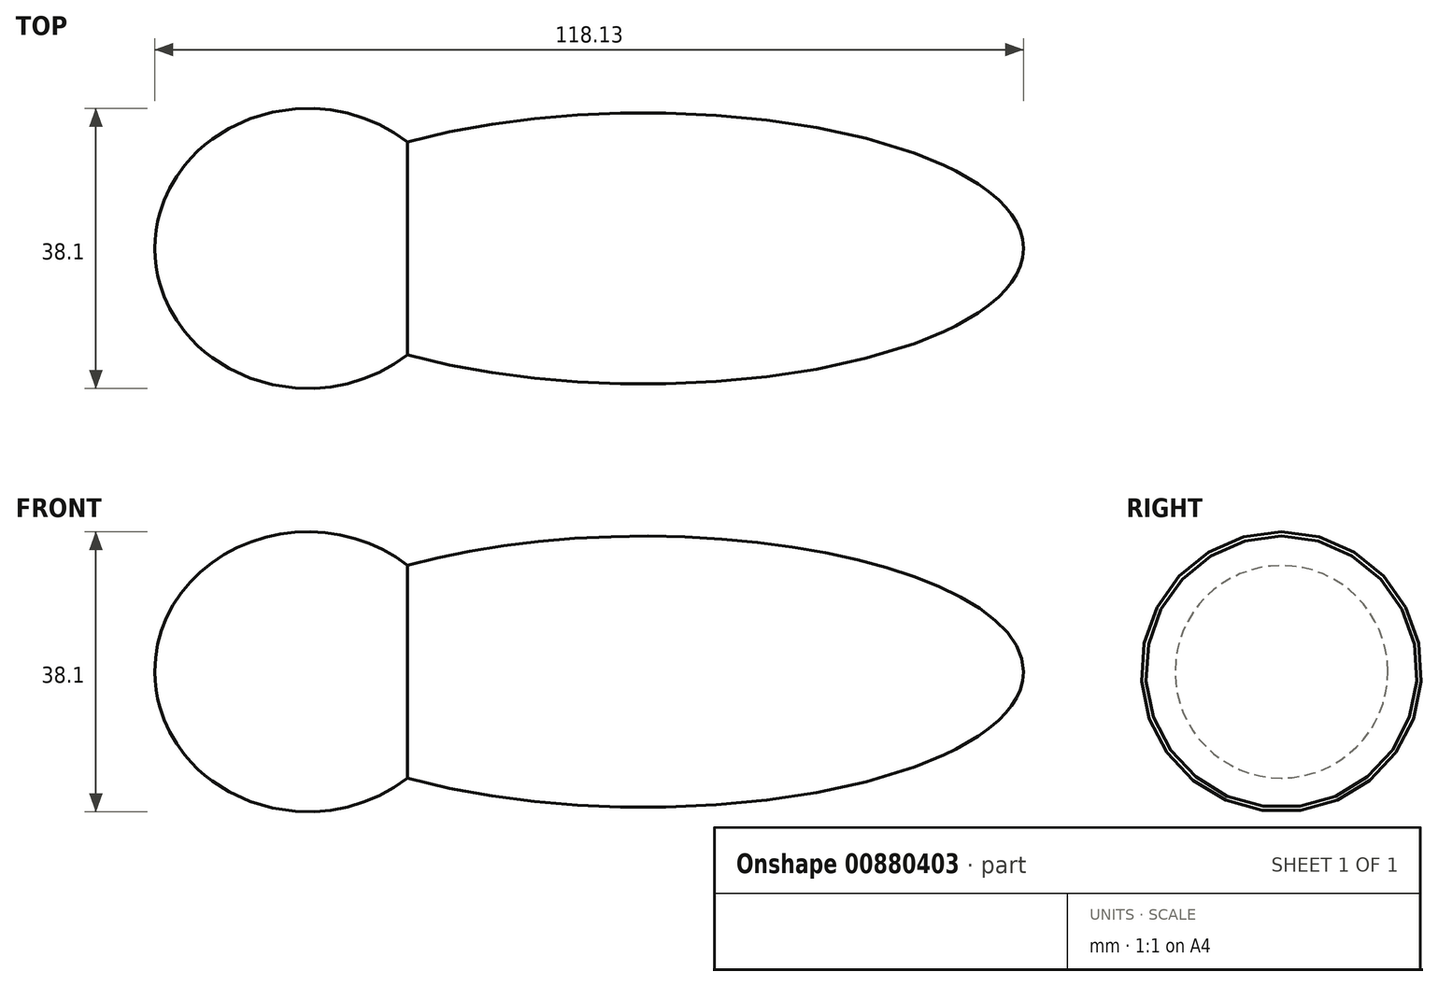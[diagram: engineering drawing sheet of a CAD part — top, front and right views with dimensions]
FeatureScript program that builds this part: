
annotation { "Feature Type Name" : "Feature", "Feature Type Description" : "" }
export const myFeature = defineFeature(function(context is Context, id is Id, definition is map)
    precondition{}
    {
        {
            var Q0;
            Q0=qCreatedBy(makeId("Front.planeOp"),FACE);
            var sketch = newSketch(context, id + "F0", { "sketchPlane" : qUnion([Q0])});
            skEllipticalArc(sketch, "E0", {});
            skLineSegment(sketch, "E1", {"start": v(-51.65, 0) * mm, "end": v(51.65, 0) * mm});
            const initialGuessF0  = {"E0": [0, 0, 1, 0, 0.05165152624249458, 0.01845279159120785, 0, 3.141592653589793]};
            skSetInitialGuess(sketch, initialGuessF0);
            skSolve(sketch);
        }
        {
            var Q0;
            Q0 = qSketchRegion(id + "F0", true);
            var Q1;
            Q1=sQuery(id+"F0.wireOp",EDGE,"E1");
            revolve(context, id + "F1", {"surfaceOperationType" : NewSurfaceOperationType.NEW, "entities" : qUnion([Q0]), "axis" : qUnion([Q1]), "revolveType" : RevolveType.FULL});
        }
        {
            var Q0;
            Q0=qCreatedBy(makeId("Front.planeOp"),FACE);
            var sketch = newSketch(context, id + "F2", { "sketchPlane" : qUnion([Q0])});
            skEllipticalArc(sketch, "E2", {});
            skLineSegment(sketch, "E3", {"start": v(-66.48, 0) * mm, "end": v(-24.83, 0) * mm});
            const initialGuessF2  = {"E2": [-0.045654021203517914, 0, 1, 0, 0.020822221413254738, 0.019049457927243354, 0, 3.141592653589793]};
            skSetInitialGuess(sketch, initialGuessF2);
            skSolve(sketch);
        }
        {
            var Q0;
            Q0 = qSketchRegion(id + "F2", true);
            var Q1;
            Q1=sQuery(id+"F2.wireOp",EDGE,"E3");
            revolve(context, id + "F3", {"operationType" : NewBodyOperationType.ADD, "surfaceOperationType" : NewSurfaceOperationType.NEW, "entities" : qUnion([Q0]), "axis" : qUnion([Q1]), "revolveType" : RevolveType.FULL});
        }
    });
